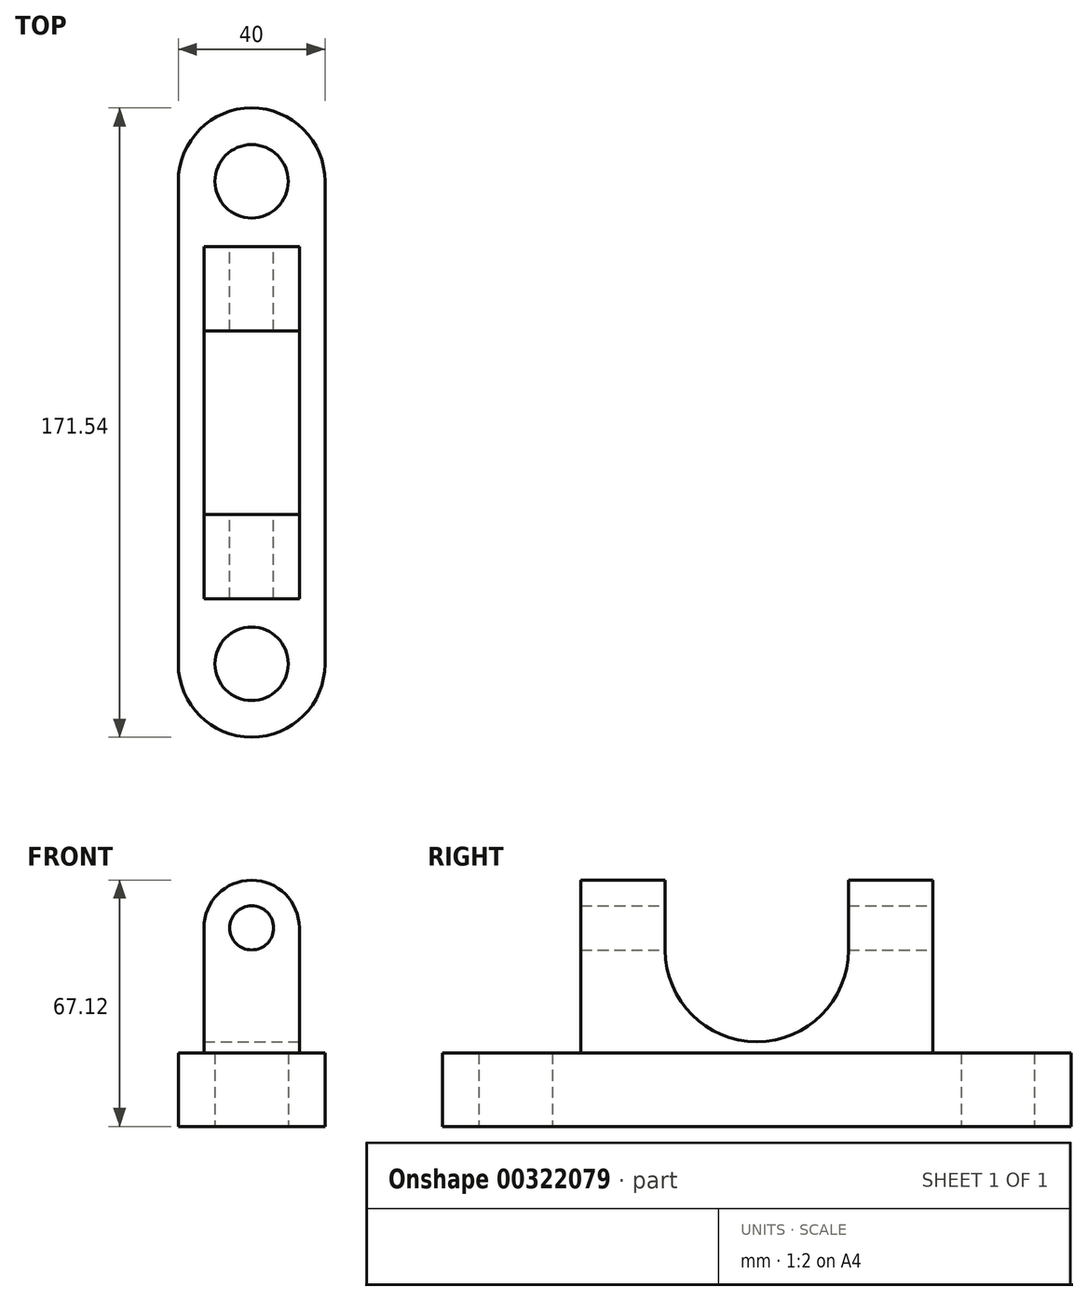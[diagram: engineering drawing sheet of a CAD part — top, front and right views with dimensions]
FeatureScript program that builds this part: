
annotation { "Feature Type Name" : "Feature", "Feature Type Description" : "" }
export const myFeature = defineFeature(function(context is Context, id is Id, definition is map)
    precondition{}
    {
        {
            var Q0;
            Q0=qCreatedBy(makeId("Top.planeOp"),FACE);
            var sketch = newSketch(context, id + "F0", { "sketchPlane" : qUnion([Q0])});
            skLineSegment(sketch, "E0.left", {"start": v(20, 65.77) * mm, "end": v(20, -65.77) * mm});
            skLineSegment(sketch, "E0.right", {"start": v(-20, 65.77) * mm, "end": v(-20, -65.77) * mm});
            skPoint(sketch, "E0.middle", {"position": v(0, 0) * mm});
            skArc(sketch, "E1", {"start": v(20, 65.77) * mm, "mid": v(0, 85.77) * mm, "end": v(-20, 65.77) * mm});
            skArc(sketch, "E2", {"start": v(-20, -65.77) * mm, "mid": v(0, -85.77) * mm, "end": v(20, -65.77) * mm});
            skCircle(sketch, "E3", {"center": v(0, 65.77) * mm, "radius": 10 * mm});
            skCircle(sketch, "E4", {"center": v(0, -65.77) * mm, "radius": 10 * mm});
            skSolve(sketch);
        }
        {
            var Q0;
            Q0=makeQuery(id+"F0.imprint","IMPRINT",FACE,{"disambiguationData":[TD([[makeQuery(id+"F0.imprint","IMPRINT",EDGE,{"derivedFrom":sQuery(id+"F0.wireOp",EDGE,"E0.left")}),-1.0]])]});
            extrude(context, id + "F1", {"entities" : qUnion([Q0]), "depth" : 20 * mm});
        }
        {
            var Q0;
            Q0=qCreatedBy(makeId("Front.planeOp"),FACE);
            var sketch = newSketch(context, id + "F2", { "sketchPlane" : qUnion([Q0])});
            skLineSegment(sketch, "E5.top", {"start": v(13, 19.12) * mm, "end": v(-13, 19.12) * mm});
            skLineSegment(sketch, "E5.left", {"start": v(13, 30.03) * mm, "end": v(13, 19.12) * mm});
            skLineSegment(sketch, "E5.right", {"start": v(-13, 30.03) * mm, "end": v(-13, 19.12) * mm});
            skPoint(sketch, "E5.middle", {"position": v(0, 24.58) * mm});
            skLineSegment(sketch, "E6.left", {"start": v(-13, 54.12) * mm, "end": v(-13, 19.12) * mm});
            skLineSegment(sketch, "E6.right", {"start": v(13, 54.12) * mm, "end": v(13, 19.12) * mm});
            skPoint(sketch, "E6.middle", {"position": v(0, 30.03) * mm});
            skPoint(sketch, "E7.orphan", {"position": v(-13, 5.95) * mm});
            skPoint(sketch, "E8.orphan", {"position": v(13, 5.95) * mm});
            skArc(sketch, "E9", {"start": v(13, 54.12) * mm, "mid": v(0, 67.12) * mm, "end": v(-13, 54.12) * mm});
            skCircle(sketch, "E10", {"center": v(0, 54.12) * mm, "radius": 6 * mm});
            skSolve(sketch);
        }
        {
            var Q0;
            {var subQ2=sQuery(id+"F2.wireOp",EDGE,"E5.top");Q0=makeQuery(id+"F2.imprint","IMPRINT",FACE,{"disambiguationData":[TD([[makeQuery(id+"F2.imprint","IMPRINT",EDGE,{"derivedFrom":subQ2}),-1.0]])]});}
            extrude(context, id + "F3", {"entities" : qUnion([Q0]), "operationType" : NewBodyOperationType.ADD, "depth" : 48 * mm, "hasSecondDirection" : true, "secondDirectionOppositeDirection" : true, "secondDirectionDepth" : 48 * mm});
        }
        {
            var Q0;
            Q0=makeQuery(id+"F3.opExtrude","SWEPT_FACE",FACE,{"disambiguationData":[OSD([sQuery(id+"F2.wireOp",EDGE,"E6.right")])]});
            var sketch = newSketch(context, id + "F4", { "sketchPlane" : qUnion([Q0])});
            skPoint(sketch, "E11.centerSnap0", {"position": v(0, 54.12) * mm});
            skArc(sketch, "E12", {"start": v(-25, 48.1) * mm, "mid": v(0, 23.1) * mm, "end": v(25, 48.1) * mm});
            skLineSegment(sketch, "E13.top", {"start": v(25, 103.1) * mm, "end": v(-25, 103.1) * mm});
            skLineSegment(sketch, "E13.left", {"start": v(25, 48.1) * mm, "end": v(25, 103.1) * mm});
            skLineSegment(sketch, "E13.right", {"start": v(-25, 48.1) * mm, "end": v(-25, 103.1) * mm});
            skPoint(sketch, "E13.middle", {"position": v(0, 71.6) * mm});
            skSolve(sketch);
        }
        {
            var Q0;
            {var subQ0=sQuery(id+"F4.wireOp",EDGE,"E12");Q0=makeQuery(id+"F4.imprint","IMPRINT",FACE,{"disambiguationData":[TD([[makeQuery(id+"F4.imprint","IMPRINT",EDGE,{"derivedFrom":subQ0}),1.0]])]});}
            var Q1;
            {var subQ0=sQuery(id+"F4.wireOp",EDGE,"E13.top");Q1=makeQuery(id+"F4.imprint","IMPRINT",FACE,{"disambiguationData":[TD([[makeQuery(id+"F4.imprint","IMPRINT",EDGE,{"derivedFrom":subQ0}),1.0]])]});}
            var Q2;
            Q2=makeQuery(id+"F3.opExtrude","SWEPT_FACE",FACE,{"disambiguationData":[OSD([sQuery(id+"F2.wireOp",EDGE,"E6.left")])]});
            extrude(context, id + "F5", {"entities" : qUnion([Q0, Q1]), "operationType" : NewBodyOperationType.REMOVE, "endBound" : BoundingType.UP_TO_SURFACE, "oppositeDirection" : true, "endBoundEntityFace" : qUnion([Q2]), "depth" : 36.2 * mm});
        }
    });
